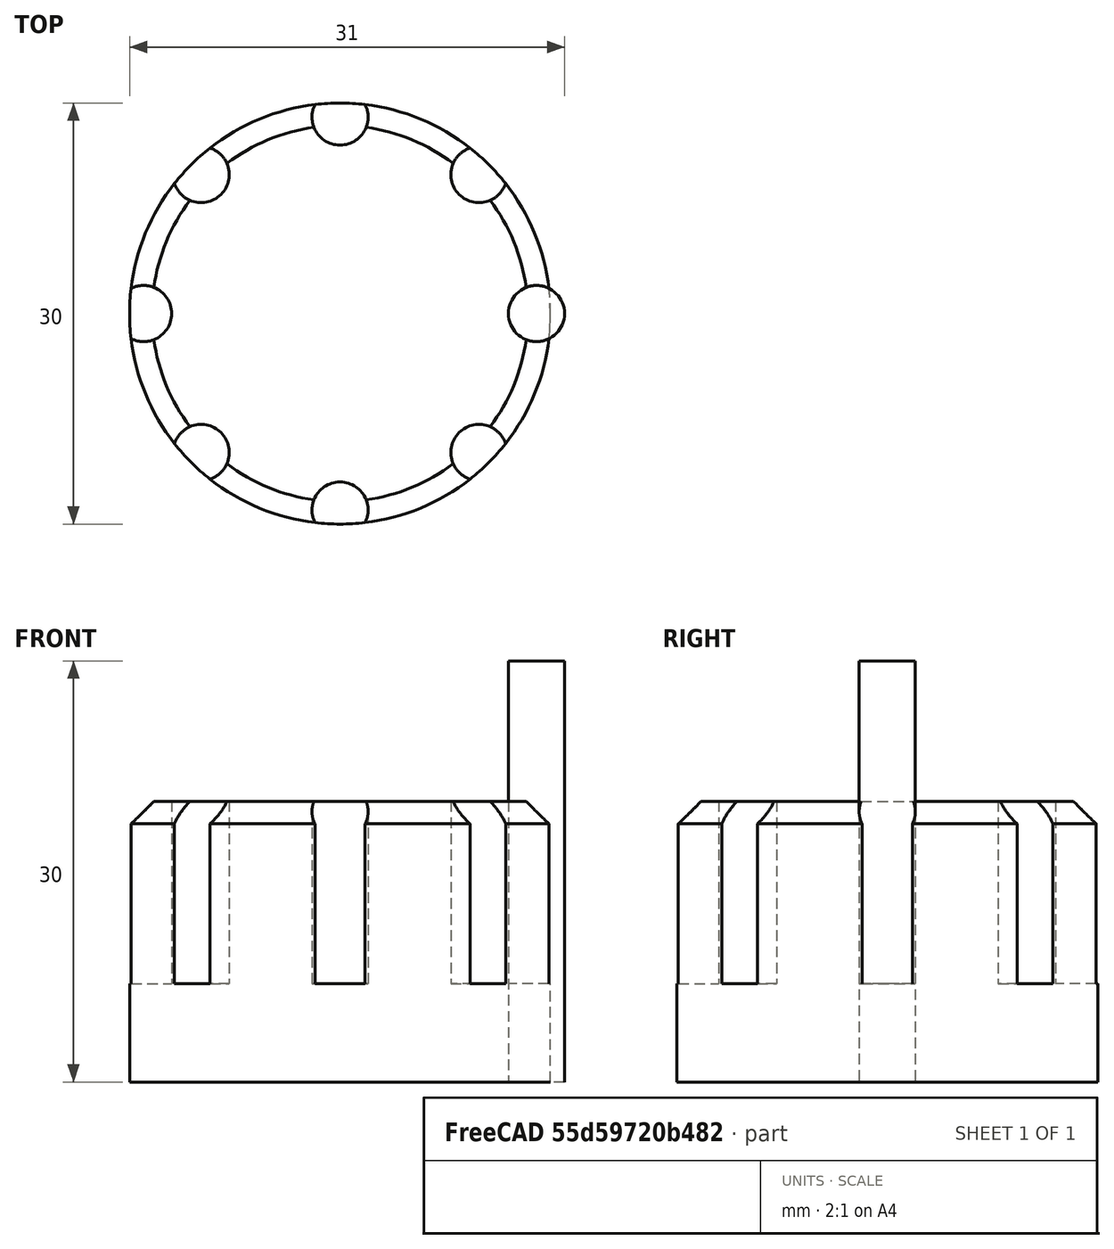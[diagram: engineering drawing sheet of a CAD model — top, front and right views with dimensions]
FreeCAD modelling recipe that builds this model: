
FCSTD DOCUMENT  (FreeCAD 0.21R33694 (Git))
Label: OJT1_T12R01_boto
License: All rights reserved
LicenseURL: http://en.wikipedia.org/wiki/All_rights_reserved
objects: Part::Cylinder×2, Part::Chamfer×1, Part::FeaturePython×1, Part::Cut×1
note: 4 computed .brp shape members not serialized (recipe doc carries the construction recipe); baked Part::Feature solids carry a one-line shape summary decoded from their .brp

FEATURE [Part::Cylinder] Cylinder
  Angle = 360
  AttacherType = Attacher::AttachEngine3D
  FirstAngle = 0
  Height = 20
  Radius = 15
  SecondAngle = 0
FEATURE [Part::Chamfer] Chamfer
  Base = -> Cylinder
  Edges = 1 edges r=1.6: [Edge3]
FEATURE [Part::Cylinder] Cylinder001
  Angle = 360
  AttacherType = Attacher::AttachEngine3D
  FirstAngle = 0
  Height = 30
  Placement = pos=(14,0,0) rot=(0,0,1;0rad)
  Radius = 2
  SecondAngle = 0
FEATURE [Part::FeaturePython] Array  # Draft array (typed FeaturePython)
  AlwaysSyncPlacement = false
  Angle = 360
  ArrayType = 1
  Axis = (0,0,1)
  Base = -> Cylinder001
  Center = (0,0,0)
  Count = 8
  ExpandArray = false
  Fuse = false
  IntervalAxis = (0,0,0)
  IntervalX = (50,0,0)
  IntervalY = (0,50,0)
  IntervalZ = (0,0,50)
  NumberCircles = 3
  NumberPolar = 8
  NumberX = 2
  NumberY = 2
  NumberZ = 1
  Placement = pos=(0,0,7) rot=(0,0,1;0rad)
  PlacementList = 8 placements: [(14,0,0),(9.89949,9.89949,0),(0,14,0),(-9.89949,9.89949,0),(-14,1.71451e-15,0),(-9.89949,-9.89949,0),(-3.10862e-15,-14,0),(9.89949,-9.89949,0)]
  RadialDistance = 50
  ScaleList = (8) [(1,1,1),(1,1,1),(1,1,1),(1,1,1),(1,1,1),(1,1,1),(1,1,1),(1,1,1)]
  Symmetry = 1
  TangentialDistance = 25
FEATURE [Part::Cut] Cut
  Base = -> Chamfer
  Refine = true
  Tool = -> Array
